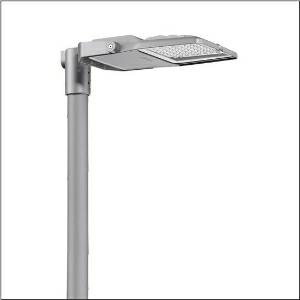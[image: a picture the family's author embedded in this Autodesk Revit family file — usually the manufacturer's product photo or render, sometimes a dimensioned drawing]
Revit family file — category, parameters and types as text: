
# Revit family: floodlight_fl_21_mini___pl64_5xa7775c2e3a_8880
name_source: partatom
category: Lighting Fixtures
units: mm (PartAtom-declared; Revit-internal decimal feet)

## family parameters
Cut with Voids When Loaded = No
Host = Face
Light Source = No
Part Type = Normal
Room Calculation Point = No
Round Connector Dimension = Use Diameter
Shared = No

## types (1)
- --- (1 x LED, 11770 lm, 89 W, 3000K)
    Apparent Load = 89 VA
    CIE Flux Codes = 28 80 98 100 100
    Color Rendering = 70
    Color Temperature = 3000K
    Default Elevation = 1800 mm
    Description = Floodlight FL 21 mini, floodlight, primary light control with lens, of PMMA, primary optical cover: protective disc, of toughened safety glass, transparent, light distribution: PL64, light emission: direct distribution, installation type: surface-mounted, LED, High Power LED, rated luminous flux: 11.770lm, luminous efficacy: 132lm/W, light colour: 730, colour temperature: 3000K, control gear: Smart Interface (Zhaga), control: flexible luminous flux parameterisation, time-dependent luminous flux control, constant luminous flux control, overheat protection, pre-setting: logarithmic dimming characteristic, with terminal, 6-pole, mains connection: 220..240V, AC, 50/60Hz, start of lifetime: 89W, end of service life: 94W, reduction: 43W, luminaire housing, of diecast aluminium, powder-coated, Siteco® metallic grey (DB 702S), corrosivity category C5 mid according to DIN EN ISO 12944, suitable for swimming pools, chlorine-resistant, sealing non-destructively replaceable, please order mast flange separately, mast bracket, of steel, galvanised, powder-coated, Siteco® metallic grey (DB 702S), Smart Interface above, protection rating (complete): IP66, insulation class (complete): insulation class II (safety insulation), certification: CE, ENEC, VDE, protection symbol: D, impact resistance: IK08, permissible operating ambient temperature: -40..+40°C, permissible operating ambient temperature for outdoor applications: -40..+50°C, standard: DIN EN 12944, LABS conformity tested according to VDMA 24364:2018-05, packaging unit: 1 piece

Light Distribution: PL64
    Height = 70 mm
    Lamp = 1 x LED
    Lamp Light Flux = 11770 lm
    Lamp Power = 89 W
    Lamp count = 1
    Length = 485 mm
    Luminous efficacy = 132 lm/W
    Manufacturer = Siteco
    ModVariant = No
    Model = 5XA7775C2E3A
    Number of Poles = 1
    OnlyDefault = Yes
    Power Factor = 1
    Product Name = Floodlight FL 21 mini | PL64
    Product group = floodlight | pylon annexe
    ProductGroupID = 6201
    Protection Class = Protection class II
    Protection Degree = IP 66
    RLX_Detail_Level = 1
    RLX_Emergency_Light_Flux = 0 lm
    RLX_Emergency_Type = 0
    RLX_Emergency_Type_DB = No
    RlxData = <blob elided: 100997 chars, md5=90129169>
    Socket = socket
    Standby Power = 0 W
    System Light Flux = 11770 lm
    System Power = 89 W
    Type Comments = factory setting: luminous flux: 100 % | dim-lin: 254 | 456 mA
    Type Image = l_1007125.jpg
    URL = http://relux.com
    VarID = @adj_186873
    Voltage = 0 V
    Weight = 0.00 kg
    Width = 337 mm

## geometry (parser evidence)
native form markers: Blend x4, Sweep x12
no freeform markers — native parametric forms only
